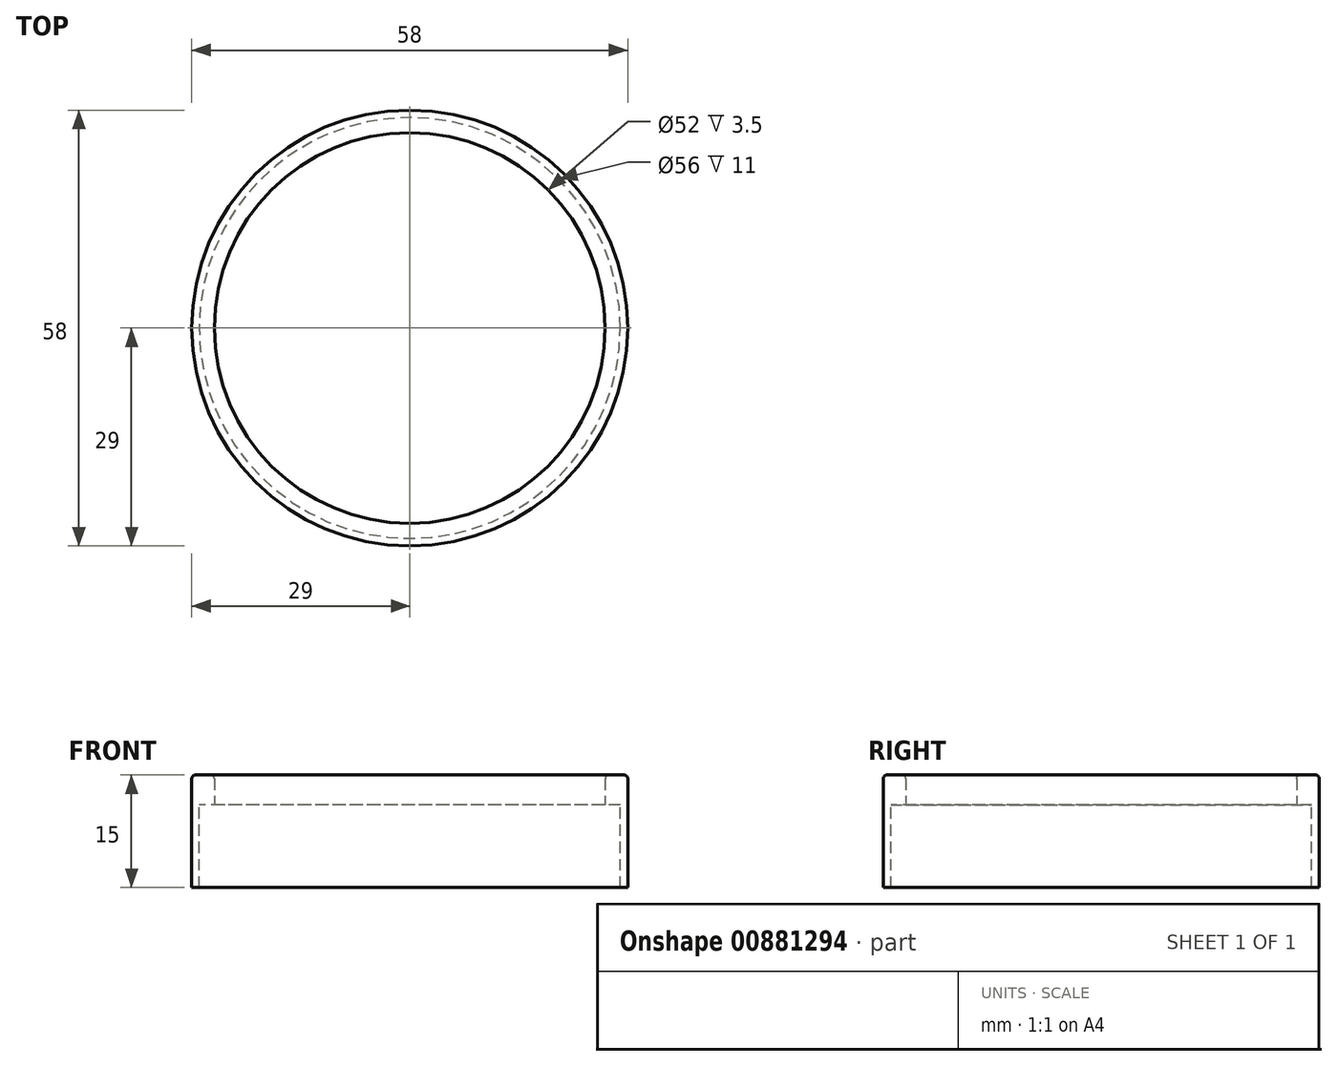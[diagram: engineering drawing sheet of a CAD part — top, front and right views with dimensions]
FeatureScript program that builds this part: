
annotation { "Feature Type Name" : "Feature", "Feature Type Description" : "" }
export const myFeature = defineFeature(function(context is Context, id is Id, definition is map)
    precondition{}
    {
        {
            var Q0;
            Q0=qCreatedBy(makeId("Top.planeOp"),FACE);
            var sketch = newSketch(context, id + "F0", { "sketchPlane" : qUnion([Q0])});
            skCircle(sketch, "E0", {"center": v(0, 0) * mm, "radius": 26 * mm});
            skCircle(sketch, "E1", {"center": v(0, 0) * mm, "radius": 30 * mm});
            skCircle(sketch, "E2", {"center": v(0, 0) * mm, "radius": 28 * mm});
            skSolve(sketch);
        }
        {
            var Q0;
            Q0=makeQuery(id+"F0.imprint","IMPRINT",FACE,{"disambiguationData":[TD([[makeQuery(id+"F0.imprint","IMPRINT",EDGE,{"derivedFrom":sQuery(id+"F0.wireOp",EDGE,"E0")}),-1.0]])]});
            extrude(context, id + "F1", {"entities" : qUnion([Q0]), "depth" : 4 * mm});
        }
        {
            var Q0;
            Q0=makeQuery(id+"F1.opExtrude","CAP_FACE",FACE,{"disambiguationData":[OSD([sQuery(id+"F0.wireOp",EDGE,"E0"),sQuery(id+"F0.wireOp",EDGE,"E2")])],"isStart":false});
            var sketch = newSketch(context, id + "F2", { "sketchPlane" : qUnion([Q0])});
            skCircle(sketch, "E3", {"center": v(0, 0) * mm, "radius": 29 * mm});
            skCircle(sketch, "E4", {"center": v(0, 0) * mm, "radius": 27.5 * mm});
            skSolve(sketch);
        }
        {
            var Q0;
            Q0=makeQuery(id+"F2.imprint","IMPRINT",FACE,{"disambiguationData":[TD([[makeQuery(id+"F2.imprint","IMPRINT",EDGE,{"derivedFrom":sQuery(id+"F2.wireOp",EDGE,"E3")}),1.0]])]});
            extrude(context, id + "F3", {"entities" : qUnion([Q0]), "operationType" : NewBodyOperationType.ADD, "oppositeDirection" : true, "depth" : 15 * mm});
        }
        {
            var Q0;
            Q0=makeQuery(id+"F1.opExtrude","CAP_EDGE",EDGE,{"disambiguationData":[OSD([sQuery(id+"F0.wireOp",EDGE,"E0")])],"isStart":false});
            var Q1;
            Q1=makeQuery(id+"F3.opExtrude","CAP_EDGE",EDGE,{"disambiguationData":[OSD([sQuery(id+"F2.wireOp",EDGE,"E3")])],"isStart":true});
            fillet(context, id + "F4", {"entities" : qUnion([Q0, Q1]), "radius" : 0.5 * mm, "tangentPropagation" : true, "allowEdgeOverflow" : false});
        }
    });
